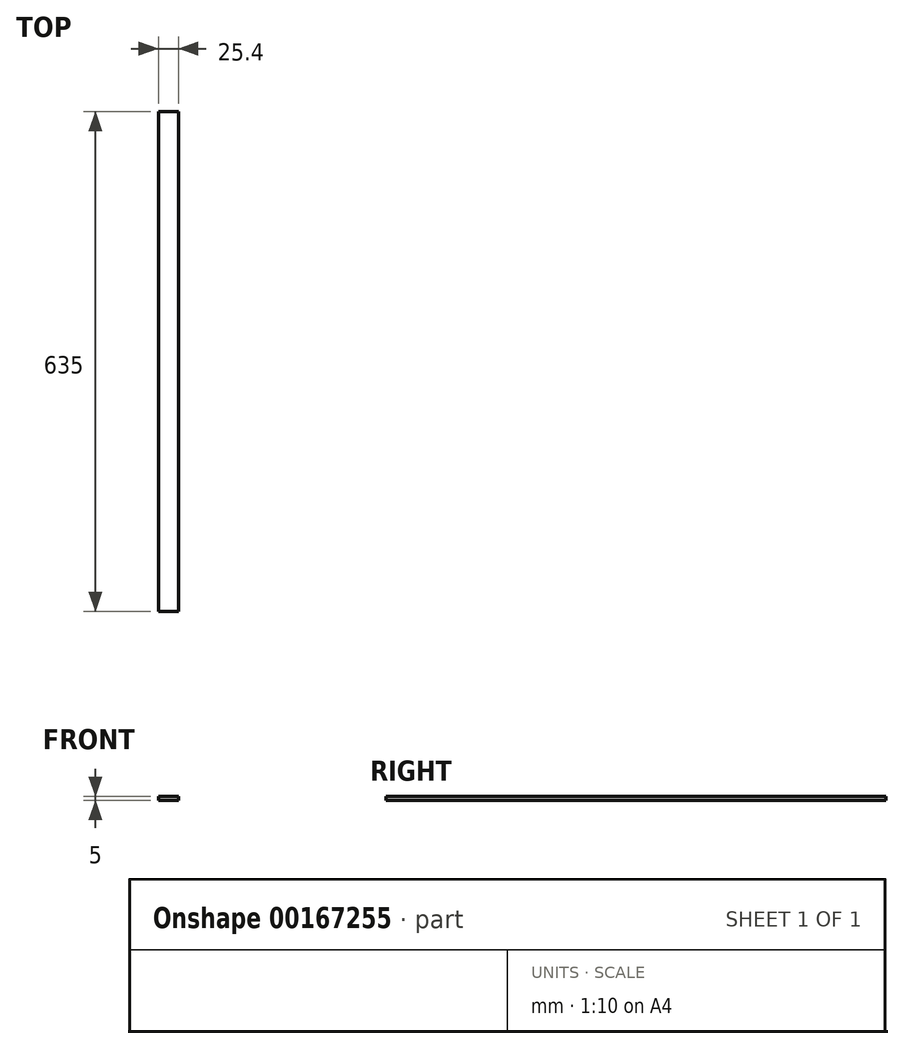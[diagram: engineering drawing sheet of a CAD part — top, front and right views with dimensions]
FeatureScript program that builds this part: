
annotation { "Feature Type Name" : "Feature", "Feature Type Description" : "" }
export const myFeature = defineFeature(function(context is Context, id is Id, definition is map)
    precondition{}
    {
        {
            var Q0;
            Q0=qCreatedBy(makeId("Top.planeOp"),FACE);
            var sketch = newSketch(context, id + "F0", { "sketchPlane" : qUnion([Q0])});
            skLineSegment(sketch, "E0.bottom", {"start": v(-10.21, 547.5) * mm, "end": v(15.19, 547.5) * mm});
            skLineSegment(sketch, "E0.top", {"start": v(-10.21, -87.5) * mm, "end": v(15.19, -87.5) * mm});
            skLineSegment(sketch, "E0.left", {"start": v(-10.21, 547.5) * mm, "end": v(-10.21, -87.5) * mm});
            skLineSegment(sketch, "E0.right", {"start": v(15.19, 547.5) * mm, "end": v(15.19, -87.5) * mm});
            skSolve(sketch);
        }
        {
            var Q0;
            Q0 = qSketchRegion(id + "F0", true);
            extrude(context, id + "F1", {"entities" : qUnion([Q0]), "depth" : 5 * mm});
        }
    });
